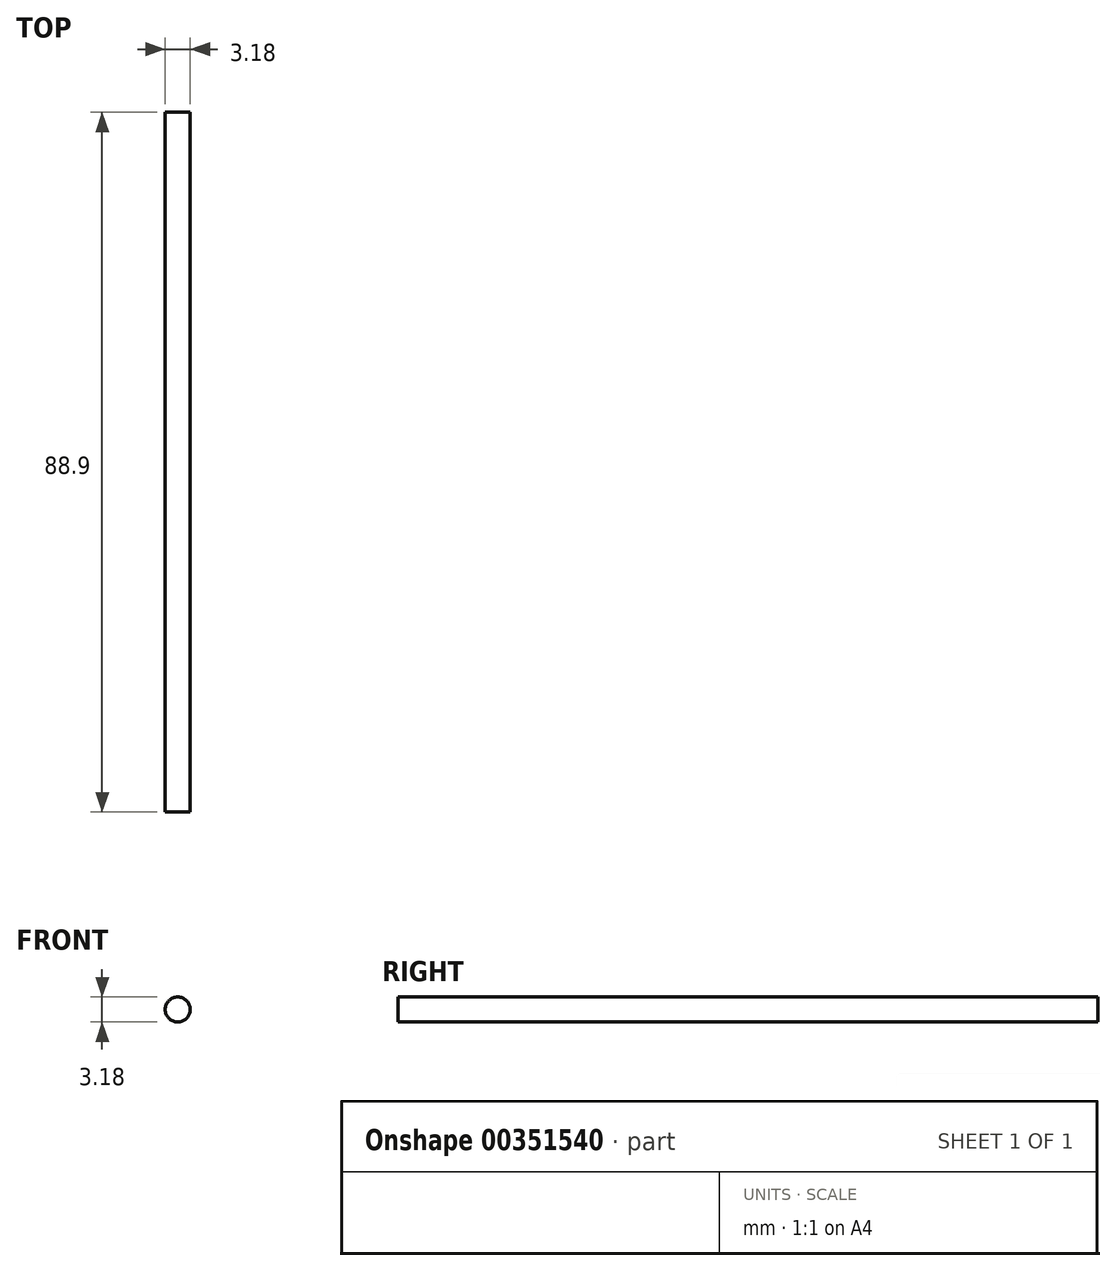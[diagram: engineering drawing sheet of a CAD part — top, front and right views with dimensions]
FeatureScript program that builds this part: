
annotation { "Feature Type Name" : "Feature", "Feature Type Description" : "" }
export const myFeature = defineFeature(function(context is Context, id is Id, definition is map)
    precondition{}
    {
        {
            var Q0;
            Q0=qCreatedBy(makeId("Front.planeOp"),FACE);
            var sketch = newSketch(context, id + "F0", { "sketchPlane" : qUnion([Q0])});
            skCircle(sketch, "E0", {"center": v(0, 0) * mm, "radius": 1.59 * mm});
            skSolve(sketch);
        }
        {
            var Q0;
            Q0 = qSketchRegion(id + "F0", true);
            extrude(context, id + "F1", {"entities" : qUnion([Q0]), "depth" : 88.9 * mm, "symmetric" : true});
        }
    });
